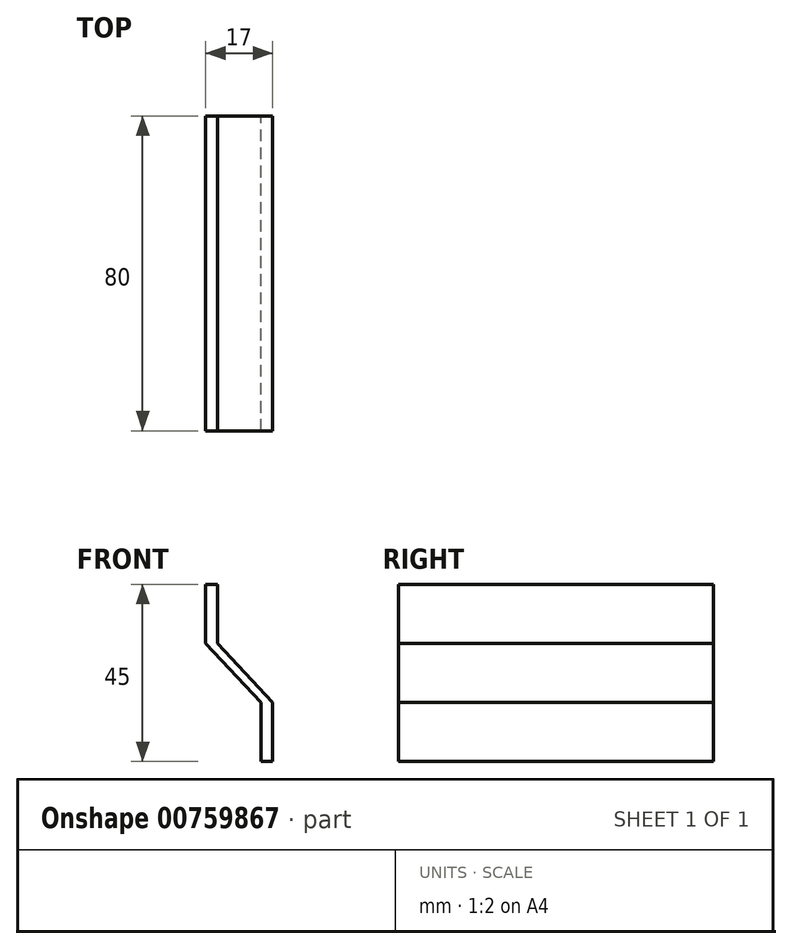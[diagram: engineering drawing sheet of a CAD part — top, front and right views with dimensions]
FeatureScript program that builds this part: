
annotation { "Feature Type Name" : "Feature", "Feature Type Description" : "" }
export const myFeature = defineFeature(function(context is Context, id is Id, definition is map)
    precondition{}
    {
        {
            var Q0;
            Q0=qCreatedBy(makeId("Front.planeOp"),FACE);
            var sketch = newSketch(context, id + "F0", { "sketchPlane" : qUnion([Q0])});
            skLineSegment(sketch, "E0", {"start": v(0, 0) * mm, "end": v(3, 0) * mm});
            skLineSegment(sketch, "E1", {"start": v(3, 0) * mm, "end": v(3, -15) * mm});
            skLineSegment(sketch, "E2", {"start": v(17, -30) * mm, "end": v(17, -45) * mm});
            skLineSegment(sketch, "E3", {"start": v(17, -45) * mm, "end": v(14, -45) * mm});
            skLineSegment(sketch, "E4", {"start": v(14, -45) * mm, "end": v(14, -30) * mm});
            skLineSegment(sketch, "E5", {"start": v(0, -15) * mm, "end": v(0, 0) * mm});
            skLineSegment(sketch, "E6", {"start": v(3, -15) * mm, "end": v(17, -30) * mm});
            skLineSegment(sketch, "E7", {"start": v(14, -30) * mm, "end": v(0, -15) * mm});
            skSolve(sketch);
        }
        {
            var Q0;
            Q0=makeQuery(id+"F0.imprint","IMPRINT",FACE,{"disambiguationData":[TD([[makeQuery(id+"F0.imprint","IMPRINT",EDGE,{"derivedFrom":sQuery(id+"F0.wireOp",EDGE,"E0")}),-1.0]])]});
            extrude(context, id + "F1", {"entities" : qUnion([Q0]), "endBound" : BoundingType.SYMMETRIC, "depth" : 80 * mm, "offsetDistance" : 25 * mm});
        }
    });
